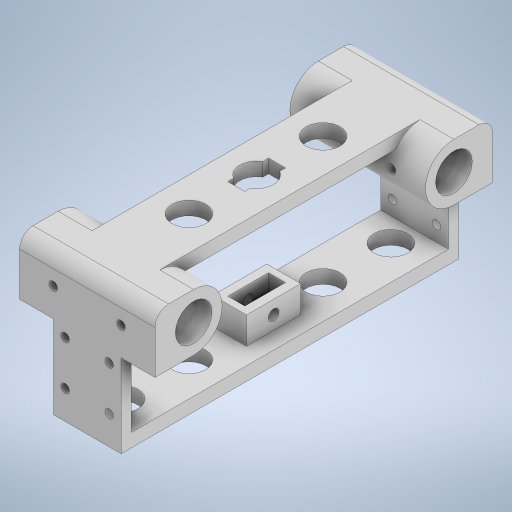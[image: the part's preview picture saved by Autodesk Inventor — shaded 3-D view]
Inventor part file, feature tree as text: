
AUTODESK INVENTOR PART (.ipt)
format: ipt  version: 2024 (Build 280153000, 153)  size: 495,616 bytes
history: native  units: mm
features: extrude x11, sketch x10, projected_geometry x7, other x1, fillet x1
ambient origin geometry x8: Origin, YZ Plane, XZ Plane, XY Plane, X Axis, Y Axis, Z Axis, Center Point
bodies: Body1 (feature_tree)
feature tree (30):
  other  "솔리드1"
  extrude  "돌출1"  Depth=30.0mm
  fillet  "모깎기1"  Radius=3.0mm
  extrude  "돌출4"  Depth=20.0mm TaperAngle=0.0deg
  extrude  "돌출5"  Depth=10.8mm
  sketch  "스케치6"
  extrude  "돌출6"  Depth=16.8mm
  extrude  "돌출7"  Depth=8.5mm
  extrude  "돌출8"  Depth=3.0mm
  extrude  "돌출9"  Depth=38.4mm
  sketch  "스케치9"
  extrude  "돌출10"  Depth=4.0mm
  sketch  "스케치11"
  extrude  "돌출16"  Depth=2.5mm
  extrude  "돌출17"  Depth=8.5mm
  extrude  "돌출18"  Depth=3.5mm
  sketch  "스케치1"
  sketch  "스케치4"
  sketch  "스케치5"
  projected_geometry  "투영된 루프1"
  projected_geometry  "투영된 루프2"
  sketch  "스케치7"
  sketch  "스케치8"
  projected_geometry  "투영된 루프3"
  projected_geometry  "투영된 루프4"
  sketch  "스케치10"
  projected_geometry  "투영된 루프5"
  projected_geometry  "투영된 루프6"
  sketch  "스케치15"
  projected_geometry  "투영된 루프8"
